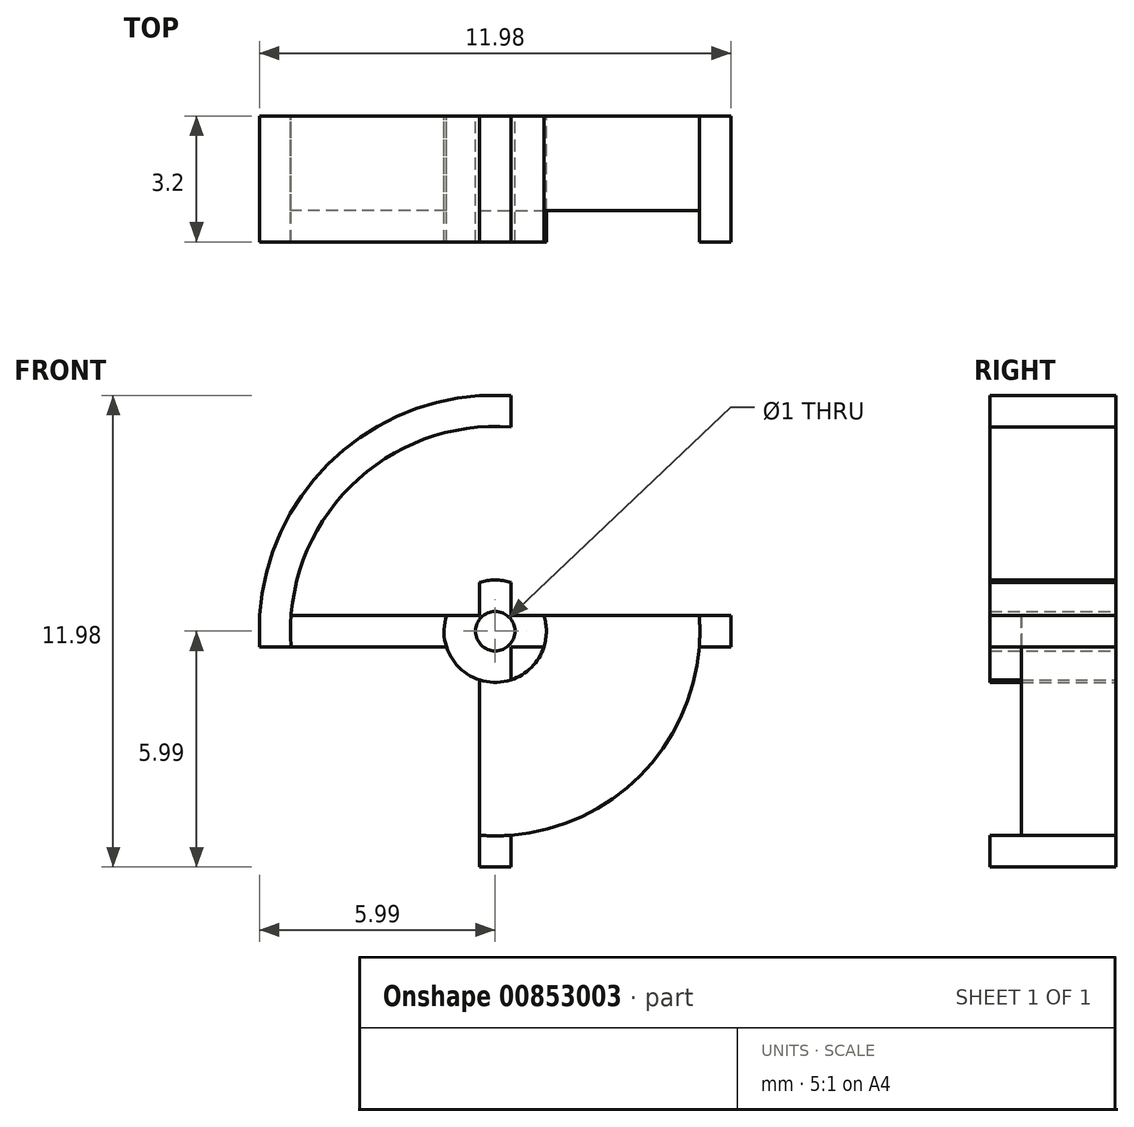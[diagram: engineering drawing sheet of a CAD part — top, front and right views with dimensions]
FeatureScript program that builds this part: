
annotation { "Feature Type Name" : "Feature", "Feature Type Description" : "" }
export const myFeature = defineFeature(function(context is Context, id is Id, definition is map)
    precondition{}
    {
        {
            var Q0;
            Q0=qCreatedBy(makeId("Front.planeOp"),FACE);
            var sketch = newSketch(context, id + "F0", { "sketchPlane" : qUnion([Q0])});
            skCircle(sketch, "E0", {"center": v(0, 0) * mm, "radius": 6 * mm});
            skCircle(sketch, "E1", {"center": v(0, 0) * mm, "radius": 5.2 * mm});
            skCircle(sketch, "E2", {"center": v(0, 0) * mm, "radius": 0.5 * mm});
            skCircle(sketch, "E3", {"center": v(0, 0) * mm, "radius": 1.3 * mm});
            skLineSegment(sketch, "E4.bottom", {"start": v(5.99, -0.4) * mm, "end": v(-5.99, -0.4) * mm});
            skLineSegment(sketch, "E4.top", {"start": v(5.99, 0.4) * mm, "end": v(-5.99, 0.4) * mm});
            skLineSegment(sketch, "E4.left", {"start": v(5.99, -0.4) * mm, "end": v(5.99, 0.4) * mm});
            skLineSegment(sketch, "E4.right", {"start": v(-5.99, -0.4) * mm, "end": v(-5.99, 0.4) * mm});
            skLineSegment(sketch, "E5.bottom", {"start": v(0.4, 5.99) * mm, "end": v(-0.4, 5.99) * mm});
            skLineSegment(sketch, "E5.top", {"start": v(0.4, -5.99) * mm, "end": v(-0.4, -5.99) * mm});
            skLineSegment(sketch, "E5.left", {"start": v(0.4, 5.99) * mm, "end": v(0.4, -5.99) * mm});
            skLineSegment(sketch, "E5.right", {"start": v(-0.4, 5.99) * mm, "end": v(-0.4, -5.99) * mm});
            skSolve(sketch);
        }
        {
            var Q0;
            {var subQ3=sQuery(id+"F0.wireOp",EDGE,"E5.right");var subQ5=sQuery(id+"F0.wireOp",EDGE,"E1");var subQ6=makeQuery(id+"F0.imprint","INTERSECT",VERTEX,{"disambiguationData":[OD(0.0)],"derivedFrom":[subQ5,subQ3]});Q0=makeQuery(id+"F0.imprint","IMPRINT",FACE,{"disambiguationData":[TD([[makeQuery(id+"F0.imprint","IMPRINT",EDGE,{"disambiguationData":[TD([[subQ6,-1.0]])],"derivedFrom":subQ5}),-1.0]])]});}
            var Q1;
            {var subQ5=sQuery(id+"F0.wireOp",EDGE,"E5.bottom");Q1=makeQuery(id+"F0.imprint","IMPRINT",FACE,{"disambiguationData":[TD([[makeQuery(id+"F0.imprint","IMPRINT",EDGE,{"derivedFrom":subQ5}),1.0]])]});}
            var Q2;
            {var subQ3=sQuery(id+"F0.wireOp",EDGE,"E5.left");var subQ5=sQuery(id+"F0.wireOp",EDGE,"E1");var subQ6=makeQuery(id+"F0.imprint","INTERSECT",VERTEX,{"disambiguationData":[OD(0.0)],"derivedFrom":[subQ5,subQ3]});Q2=makeQuery(id+"F0.imprint","IMPRINT",FACE,{"disambiguationData":[TD([[makeQuery(id+"F0.imprint","IMPRINT",EDGE,{"disambiguationData":[TD([[subQ6,1.0]])],"derivedFrom":subQ5}),-1.0]])]});}
            var Q3;
            {var subQ5=sQuery(id+"F0.wireOp",EDGE,"E4.left");Q3=makeQuery(id+"F0.imprint","IMPRINT",FACE,{"disambiguationData":[TD([[makeQuery(id+"F0.imprint","IMPRINT",EDGE,{"derivedFrom":subQ5}),1.0]])]});}
            var Q4;
            {var subQ3=sQuery(id+"F0.wireOp",EDGE,"E5.left");var subQ5=sQuery(id+"F0.wireOp",EDGE,"E1");var subQ6=makeQuery(id+"F0.imprint","INTERSECT",VERTEX,{"disambiguationData":[OD(1.0)],"derivedFrom":[subQ5,subQ3]});Q4=makeQuery(id+"F0.imprint","IMPRINT",FACE,{"disambiguationData":[TD([[makeQuery(id+"F0.imprint","IMPRINT",EDGE,{"disambiguationData":[TD([[subQ6,-1.0]])],"derivedFrom":subQ5}),-1.0]])]});}
            var Q5;
            {var subQ5=sQuery(id+"F0.wireOp",EDGE,"E5.top");Q5=makeQuery(id+"F0.imprint","IMPRINT",FACE,{"disambiguationData":[TD([[makeQuery(id+"F0.imprint","IMPRINT",EDGE,{"derivedFrom":subQ5}),-1.0]])]});}
            var Q6;
            {var subQ0=sQuery(id+"F0.wireOp",EDGE,"E4.bottom");var subQ5=sQuery(id+"F0.wireOp",EDGE,"E1");var subQ6=makeQuery(id+"F0.imprint","INTERSECT",VERTEX,{"disambiguationData":[OD(0.0)],"derivedFrom":[subQ5,subQ0]});Q6=makeQuery(id+"F0.imprint","IMPRINT",FACE,{"disambiguationData":[TD([[makeQuery(id+"F0.imprint","IMPRINT",EDGE,{"disambiguationData":[TD([[subQ6,-1.0]])],"derivedFrom":subQ5}),-1.0]])]});}
            var Q7;
            {var subQ5=sQuery(id+"F0.wireOp",EDGE,"E4.right");Q7=makeQuery(id+"F0.imprint","IMPRINT",FACE,{"disambiguationData":[TD([[makeQuery(id+"F0.imprint","IMPRINT",EDGE,{"derivedFrom":subQ5}),-1.0]])]});}
            var Q8;
            {var subQ0=sQuery(id+"F0.wireOp",EDGE,"E5.right");var subQ1=sQuery(id+"F0.wireOp",EDGE,"E3");var subQ2=makeQuery(id+"F0.imprint","INTERSECT",VERTEX,{"disambiguationData":[OD(0.0)],"derivedFrom":[subQ1,subQ0]});Q8=makeQuery(id+"F0.imprint","IMPRINT",FACE,{"disambiguationData":[TD([[makeQuery(id+"F0.imprint","IMPRINT",EDGE,{"disambiguationData":[TD([[subQ2,-1.0]])],"derivedFrom":subQ1}),1.0]])]});}
            var Q9;
            {var subQ0=sQuery(id+"F0.wireOp",EDGE,"E4.top");var subQ1=sQuery(id+"F0.wireOp",EDGE,"E2");var subQ5=makeQuery(id+"F0.imprint","INTERSECT",VERTEX,{"disambiguationData":[OD(0.0)],"derivedFrom":[subQ1,subQ0]});Q9=makeQuery(id+"F0.imprint","IMPRINT",FACE,{"disambiguationData":[TD([[makeQuery(id+"F0.imprint","IMPRINT",EDGE,{"disambiguationData":[TD([[subQ5,-1.0]])],"derivedFrom":subQ1}),-1.0]])]});}
            var Q10;
            {var subQ0=sQuery(id+"F0.wireOp",EDGE,"E5.left");var subQ1=sQuery(id+"F0.wireOp",EDGE,"E3");var subQ2=makeQuery(id+"F0.imprint","INTERSECT",VERTEX,{"disambiguationData":[OD(0.0)],"derivedFrom":[subQ1,subQ0]});Q10=makeQuery(id+"F0.imprint","IMPRINT",FACE,{"disambiguationData":[TD([[makeQuery(id+"F0.imprint","IMPRINT",EDGE,{"disambiguationData":[TD([[subQ2,1.0]])],"derivedFrom":subQ1}),1.0]])]});}
            var Q11;
            {var subQ3=sQuery(id+"F0.wireOp",EDGE,"E5.left");var subQ5=sQuery(id+"F0.wireOp",EDGE,"E2");var subQ6=makeQuery(id+"F0.imprint","INTERSECT",VERTEX,{"disambiguationData":[OD(0.0)],"derivedFrom":[subQ5,subQ3]});Q11=makeQuery(id+"F0.imprint","IMPRINT",FACE,{"disambiguationData":[TD([[makeQuery(id+"F0.imprint","IMPRINT",EDGE,{"disambiguationData":[TD([[subQ6,1.0]])],"derivedFrom":subQ5}),-1.0]])]});}
            var Q12;
            {var subQ0=sQuery(id+"F0.wireOp",EDGE,"E5.left");var subQ1=sQuery(id+"F0.wireOp",EDGE,"E3");var subQ2=makeQuery(id+"F0.imprint","INTERSECT",VERTEX,{"disambiguationData":[OD(1.0)],"derivedFrom":[subQ1,subQ0]});Q12=makeQuery(id+"F0.imprint","IMPRINT",FACE,{"disambiguationData":[TD([[makeQuery(id+"F0.imprint","IMPRINT",EDGE,{"disambiguationData":[TD([[subQ2,-1.0]])],"derivedFrom":subQ1}),1.0]])]});}
            var Q13;
            {var subQ0=sQuery(id+"F0.wireOp",EDGE,"E4.bottom");var subQ1=sQuery(id+"F0.wireOp",EDGE,"E2");var subQ2=makeQuery(id+"F0.imprint","INTERSECT",VERTEX,{"disambiguationData":[OD(0.0)],"derivedFrom":[subQ1,subQ0]});Q13=makeQuery(id+"F0.imprint","IMPRINT",FACE,{"disambiguationData":[TD([[makeQuery(id+"F0.imprint","IMPRINT",EDGE,{"disambiguationData":[TD([[subQ2,-1.0]])],"derivedFrom":subQ1}),-1.0]])]});}
            var Q14;
            {var subQ0=sQuery(id+"F0.wireOp",EDGE,"E4.bottom");var subQ1=sQuery(id+"F0.wireOp",EDGE,"E3");var subQ2=makeQuery(id+"F0.imprint","INTERSECT",VERTEX,{"disambiguationData":[OD(0.0)],"derivedFrom":[subQ1,subQ0]});Q14=makeQuery(id+"F0.imprint","IMPRINT",FACE,{"disambiguationData":[TD([[makeQuery(id+"F0.imprint","IMPRINT",EDGE,{"disambiguationData":[TD([[subQ2,-1.0]])],"derivedFrom":subQ1}),1.0]])]});}
            var Q15;
            {var subQ3=sQuery(id+"F0.wireOp",EDGE,"E5.right");var subQ8=sQuery(id+"F0.wireOp",EDGE,"E2");var subQ9=makeQuery(id+"F0.imprint","INTERSECT",VERTEX,{"disambiguationData":[OD(0.0)],"derivedFrom":[subQ8,subQ3]});Q15=makeQuery(id+"F0.imprint","IMPRINT",FACE,{"disambiguationData":[TD([[makeQuery(id+"F0.imprint","IMPRINT",EDGE,{"disambiguationData":[TD([[subQ9,-1.0]])],"derivedFrom":subQ8}),-1.0]])]});}
            var Q16;
            {var subQ0=sQuery(id+"F0.wireOp",EDGE,"E4.top");var subQ1=sQuery(id+"F0.wireOp",EDGE,"E2");var subQ2=makeQuery(id+"F0.imprint","INTERSECT",VERTEX,{"disambiguationData":[OD(1.0)],"derivedFrom":[subQ1,subQ0]});Q16=makeQuery(id+"F0.imprint","IMPRINT",FACE,{"disambiguationData":[TD([[makeQuery(id+"F0.imprint","IMPRINT",EDGE,{"disambiguationData":[TD([[subQ2,-1.0]])],"derivedFrom":subQ1}),-1.0]])]});}
            var Q17;
            {var subQ0=sQuery(id+"F0.wireOp",EDGE,"E4.top");var subQ1=sQuery(id+"F0.wireOp",EDGE,"E2");var subQ2=makeQuery(id+"F0.imprint","INTERSECT",VERTEX,{"disambiguationData":[OD(0.0)],"derivedFrom":[subQ1,subQ0]});Q17=makeQuery(id+"F0.imprint","IMPRINT",FACE,{"disambiguationData":[TD([[makeQuery(id+"F0.imprint","IMPRINT",EDGE,{"disambiguationData":[TD([[subQ2,1.0]])],"derivedFrom":subQ1}),-1.0]])]});}
            var Q18;
            {var subQ0=sQuery(id+"F0.wireOp",EDGE,"E4.bottom");var subQ1=sQuery(id+"F0.wireOp",EDGE,"E2");var subQ2=makeQuery(id+"F0.imprint","INTERSECT",VERTEX,{"disambiguationData":[OD(1.0)],"derivedFrom":[subQ1,subQ0]});Q18=makeQuery(id+"F0.imprint","IMPRINT",FACE,{"disambiguationData":[TD([[makeQuery(id+"F0.imprint","IMPRINT",EDGE,{"disambiguationData":[TD([[subQ2,-1.0]])],"derivedFrom":subQ1}),-1.0]])]});}
            var Q19;
            {var subQ0=sQuery(id+"F0.wireOp",EDGE,"E5.right");var subQ1=sQuery(id+"F0.wireOp",EDGE,"E2");var subQ2=makeQuery(id+"F0.imprint","INTERSECT",VERTEX,{"disambiguationData":[OD(1.0)],"derivedFrom":[subQ1,subQ0]});Q19=makeQuery(id+"F0.imprint","IMPRINT",FACE,{"disambiguationData":[TD([[makeQuery(id+"F0.imprint","IMPRINT",EDGE,{"disambiguationData":[TD([[subQ2,-1.0]])],"derivedFrom":subQ1}),-1.0]])]});}
            extrude(context, id + "F1", {"entities" : qUnion([Q0, Q1, Q2, Q3, Q4, Q5, Q6, Q7, Q8, Q9, Q10, Q11, Q12, Q13, Q14, Q15, Q16, Q17, Q18, Q19]), "depth" : 3.2 * mm, "offsetDistance" : 25 * mm});
        }
        {
            var Q0;
            {var subQ0=sQuery(id+"F0.wireOp",EDGE,"E4.top");var subQ1=sQuery(id+"F0.wireOp",EDGE,"E1");var subQ2=makeQuery(id+"F0.imprint","INTERSECT",VERTEX,{"disambiguationData":[OD(1.0)],"derivedFrom":[subQ1,subQ0]});Q0=makeQuery(id+"F0.imprint","IMPRINT",FACE,{"disambiguationData":[TD([[makeQuery(id+"F0.imprint","IMPRINT",EDGE,{"disambiguationData":[TD([[subQ2,-1.0]])],"derivedFrom":subQ1}),1.0]])]});}
            var Q1;
            {var subQ0=sQuery(id+"F0.wireOp",EDGE,"E5.left");var subQ1=sQuery(id+"F0.wireOp",EDGE,"E1");var subQ2=makeQuery(id+"F0.imprint","INTERSECT",VERTEX,{"disambiguationData":[OD(0.0)],"derivedFrom":[subQ1,subQ0]});Q1=makeQuery(id+"F0.imprint","IMPRINT",FACE,{"disambiguationData":[TD([[makeQuery(id+"F0.imprint","IMPRINT",EDGE,{"disambiguationData":[TD([[subQ2,-1.0]])],"derivedFrom":subQ1}),1.0]])]});}
            var Q2;
            {var subQ0=sQuery(id+"F0.wireOp",EDGE,"E4.top");var subQ1=sQuery(id+"F0.wireOp",EDGE,"E1");var subQ2=makeQuery(id+"F0.imprint","INTERSECT",VERTEX,{"disambiguationData":[OD(0.0)],"derivedFrom":[subQ1,subQ0]});Q2=makeQuery(id+"F0.imprint","IMPRINT",FACE,{"disambiguationData":[TD([[makeQuery(id+"F0.imprint","IMPRINT",EDGE,{"disambiguationData":[TD([[subQ2,1.0]])],"derivedFrom":subQ1}),1.0]])]});}
            var Q3;
            {var subQ0=sQuery(id+"F0.wireOp",EDGE,"E5.right");var subQ1=sQuery(id+"F0.wireOp",EDGE,"E1");var subQ2=makeQuery(id+"F0.imprint","INTERSECT",VERTEX,{"disambiguationData":[OD(1.0)],"derivedFrom":[subQ1,subQ0]});Q3=makeQuery(id+"F0.imprint","IMPRINT",FACE,{"disambiguationData":[TD([[makeQuery(id+"F0.imprint","IMPRINT",EDGE,{"disambiguationData":[TD([[subQ2,-1.0]])],"derivedFrom":subQ1}),1.0]])]});}
            extrude(context, id + "F2", {"entities" : qUnion([Q0, Q1, Q2, Q3]), "depth" : 2.4 * mm, "offsetDistance" : 25 * mm});
        }
    });
